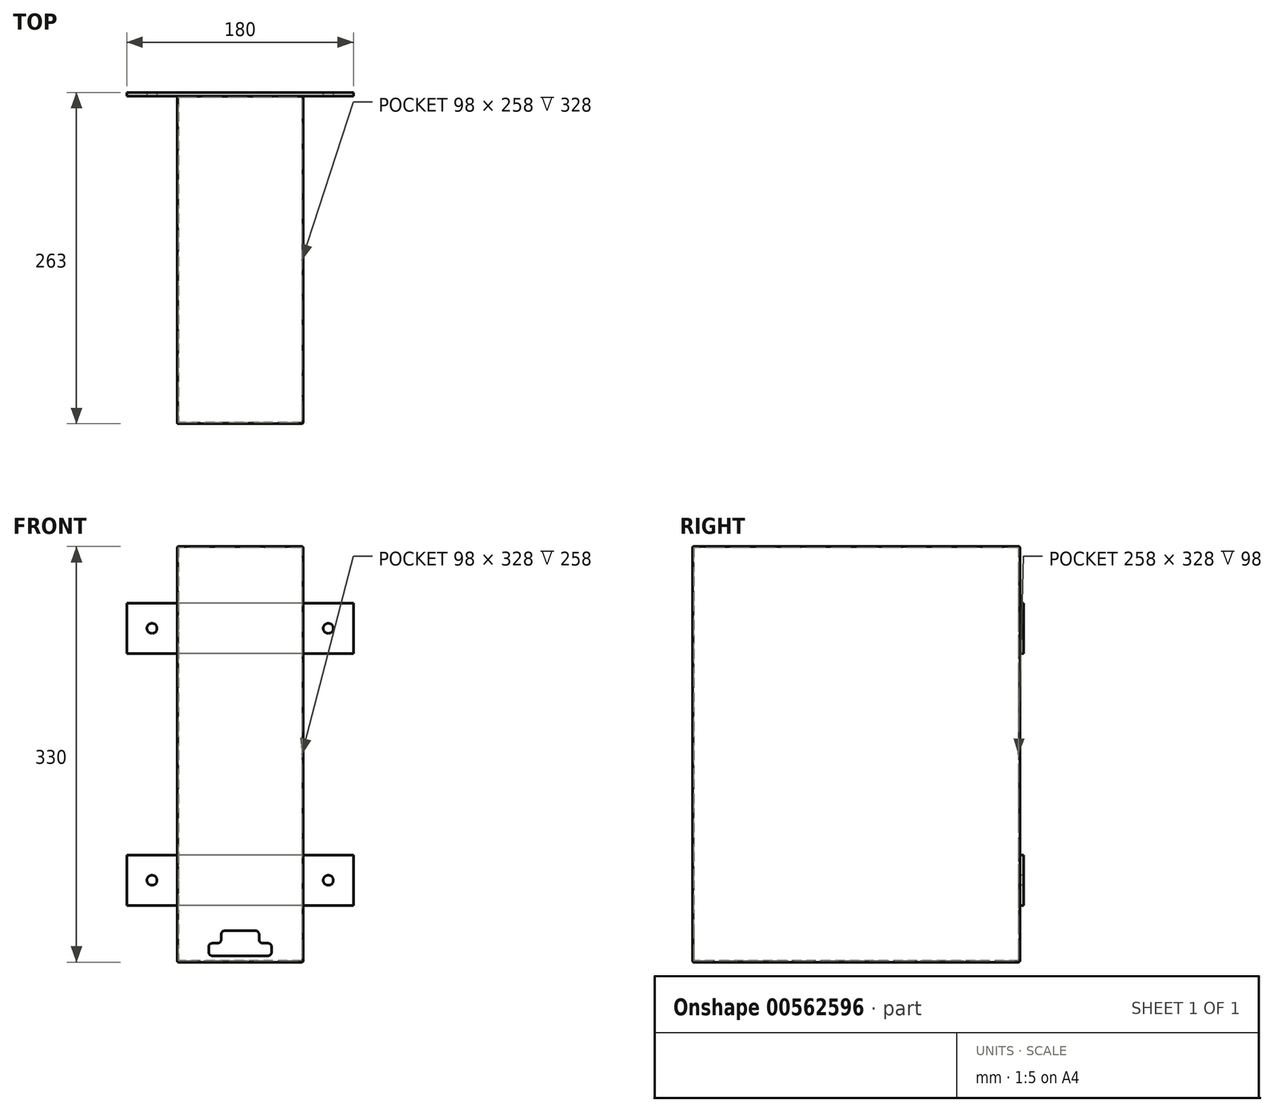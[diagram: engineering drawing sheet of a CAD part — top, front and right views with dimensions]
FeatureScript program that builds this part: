
annotation { "Feature Type Name" : "Feature", "Feature Type Description" : "" }
export const myFeature = defineFeature(function(context is Context, id is Id, definition is map)
    precondition{}
    {
        {
            var Q0;
            Q0=qCreatedBy(makeId("Top.planeOp"),FACE);
            var sketch = newSketch(context, id + "F0", { "sketchPlane" : qUnion([Q0])});
            skLineSegment(sketch, "E0.bottom", {"start": v(50, 130) * mm, "end": v(-50, 130) * mm});
            skLineSegment(sketch, "E0.top", {"start": v(50, -130) * mm, "end": v(-50, -130) * mm});
            skLineSegment(sketch, "E0.left", {"start": v(50, 130) * mm, "end": v(50, -130) * mm});
            skLineSegment(sketch, "E0.right", {"start": v(-50, 130) * mm, "end": v(-50, -130) * mm});
            skPoint(sketch, "E0.middle", {"position": v(0, 0) * mm});
            skSolve(sketch);
        }
        {
            var Q0;
            Q0=qSketchRegion(id+"F0",true);
            extrude(context, id + "F1", {"entities" : qUnion([Q0]), "endBound" : BoundingType.SYMMETRIC, "depth" : 330 * mm, "offsetDistance" : 25 * mm});
        }
        {
            var Q0;
            Q0=makeQuery(id+"F1.opExtrude","SWEPT_FACE",FACE,{"disambiguationData":[OSD([sQuery(id+"F0.wireOp",EDGE,"E0.left")])]});
            var Q1;
            Q1=makeQuery(id+"F1.opExtrude","SWEPT_FACE",FACE,{"disambiguationData":[OSD([sQuery(id+"F0.wireOp",EDGE,"E0.top")])]});
            var Q2;
            Q2=makeQuery(id+"F1.opExtrude","CAP_FACE",FACE,{"disambiguationData":[OSD([sQuery(id+"F0.wireOp",EDGE,"E0.bottom"),sQuery(id+"F0.wireOp",EDGE,"E0.top"),sQuery(id+"F0.wireOp",EDGE,"E0.left"),sQuery(id+"F0.wireOp",EDGE,"E0.right")])],"isStart":false});
            var Q3;
            Q3=makeQuery(id+"F1.opExtrude","SWEPT_FACE",FACE,{"disambiguationData":[OSD([sQuery(id+"F0.wireOp",EDGE,"E0.right")])]});
            var Q4;
            Q4=makeQuery(id+"F1.opExtrude","SWEPT_BODY",BODY,{"disambiguationData":[OSD([sQuery(id+"F0.wireOp",EDGE,"E0.bottom"),sQuery(id+"F0.wireOp",EDGE,"E0.top"),sQuery(id+"F0.wireOp",EDGE,"E0.left"),sQuery(id+"F0.wireOp",EDGE,"E0.right")])]});
            shell(context, id + "F2", {"isHollow" : true, "entities" : qUnion([Q0, Q1, Q2, Q3]), "parts" : qUnion([Q4]), "thickness" : 1 * mm});
        }
        {
            var Q0;
            Q0=makeQuery(id+"F1.opExtrude","SWEPT_FACE",FACE,{"disambiguationData":[OSD([sQuery(id+"F0.wireOp",EDGE,"E0.top")])]});
            var sketch = newSketch(context, id + "F3", { "sketchPlane" : qUnion([Q0])});
            skPoint(sketch, "E1.orphan", {"position": v(50, -165) * mm});
            skLineSegment(sketch, "E2.bottom", {"start": v(-22, -150) * mm, "end": v(-18, -150) * mm});
            skLineSegment(sketch, "E2.top", {"start": v(-22, -160) * mm, "end": v(22, -160) * mm});
            skLineSegment(sketch, "E2.left", {"start": v(-25, -153) * mm, "end": v(-25, -157) * mm});
            skLineSegment(sketch, "E2.right", {"start": v(25, -153) * mm, "end": v(25, -157) * mm});
            skLineSegment(sketch, "E3", {"start": v(-15, -147) * mm, "end": v(-15, -143) * mm});
            skLineSegment(sketch, "E4", {"start": v(-12, -140) * mm, "end": v(12, -140) * mm});
            skLineSegment(sketch, "E5", {"start": v(15, -143) * mm, "end": v(15, -147) * mm});
            skLineSegment(sketch, "E6.trimOffspring", {"start": v(18, -150) * mm, "end": v(22, -150) * mm});
            skPoint(sketch, "E7.visualSharp", {"position": v(-15, -140) * mm});
            skArc(sketch, "E7.filletArc", {"start": v(-12, -140) * mm, "mid": v(-14.12, -140.88) * mm, "end": v(-15, -143) * mm});
            skPoint(sketch, "E8.visualSharp", {"position": v(15, -140) * mm});
            skArc(sketch, "E8.filletArc", {"start": v(15, -143) * mm, "mid": v(14.12, -140.88) * mm, "end": v(12, -140) * mm});
            skPoint(sketch, "E9.visualSharp", {"position": v(15, -150) * mm});
            skArc(sketch, "E9.filletArc", {"start": v(15, -147) * mm, "mid": v(15.88, -149.12) * mm, "end": v(18, -150) * mm});
            skPoint(sketch, "E10.visualSharp", {"position": v(-15, -150) * mm});
            skArc(sketch, "E10.filletArc", {"start": v(-18, -150) * mm, "mid": v(-15.88, -149.12) * mm, "end": v(-15, -147) * mm});
            skPoint(sketch, "E11.visualSharp", {"position": v(25, -150) * mm});
            skArc(sketch, "E11.filletArc", {"start": v(25, -153) * mm, "mid": v(24.12, -150.88) * mm, "end": v(22, -150) * mm});
            skPoint(sketch, "E12.visualSharp", {"position": v(25, -160) * mm});
            skArc(sketch, "E12.filletArc", {"start": v(22, -160) * mm, "mid": v(24.12, -159.12) * mm, "end": v(25, -157) * mm});
            skPoint(sketch, "E13.visualSharp", {"position": v(-25, -160) * mm});
            skArc(sketch, "E13.filletArc", {"start": v(-25, -157) * mm, "mid": v(-24.12, -159.12) * mm, "end": v(-22, -160) * mm});
            skPoint(sketch, "E14.visualSharp", {"position": v(-25, -150) * mm});
            skArc(sketch, "E14.filletArc", {"start": v(-22, -150) * mm, "mid": v(-24.12, -150.88) * mm, "end": v(-25, -153) * mm});
            skSolve(sketch);
        }
        {
            var Q0;
            Q0=qSketchRegion(id+"F3",true);
            extrude(context, id + "F4", {"entities" : qUnion([Q0]), "operationType" : NewBodyOperationType.REMOVE, "endBound" : BoundingType.SYMMETRIC, "oppositeDirection" : true, "depth" : 440 * mm, "offsetDistance" : 25 * mm});
        }
        {
            var Q0;
            Q0=makeQuery(id+"F1.opExtrude","SWEPT_FACE",FACE,{"disambiguationData":[OSD([sQuery(id+"F0.wireOp",EDGE,"E0.left")])]});
            var Q1;
            Q1=makeQuery(id+"F1.opExtrude","CAP_FACE",FACE,{"disambiguationData":[OSD([sQuery(id+"F0.wireOp",EDGE,"E0.bottom"),sQuery(id+"F0.wireOp",EDGE,"E0.top"),sQuery(id+"F0.wireOp",EDGE,"E0.left"),sQuery(id+"F0.wireOp",EDGE,"E0.right")])],"isStart":false});
            var Q2;
            Q2=makeQuery(id+"F1.opExtrude","SWEPT_FACE",FACE,{"disambiguationData":[OSD([sQuery(id+"F0.wireOp",EDGE,"E0.right")])]});
            var Q3;
            Q3=makeQuery(id+"F1.opExtrude","CAP_FACE",FACE,{"disambiguationData":[OSD([sQuery(id+"F0.wireOp",EDGE,"E0.bottom"),sQuery(id+"F0.wireOp",EDGE,"E0.top"),sQuery(id+"F0.wireOp",EDGE,"E0.left"),sQuery(id+"F0.wireOp",EDGE,"E0.right")])],"isStart":true});
            var Q4;
            Q4=makeQuery(id+"F1.opExtrude","SWEPT_FACE",FACE,{"disambiguationData":[OSD([sQuery(id+"F0.wireOp",EDGE,"E0.bottom")])]});
            fillet(context, id + "F5", {"entities" : qUnion([Q0, Q1, Q2, Q3, Q4]), "radius" : 1 * mm, "tangentPropagation" : true, "allowEdgeOverflow" : false});
        }
        {
            var Q0;
            Q0=makeQuery(id+"F1.opExtrude","SWEPT_FACE",FACE,{"disambiguationData":[OSD([sQuery(id+"F0.wireOp",EDGE,"E0.bottom")])]});
            var sketch = newSketch(context, id + "F6", { "sketchPlane" : qUnion([Q0])});
            skLineSegment(sketch, "E15.bottom", {"start": v(-90, 120) * mm, "end": v(90, 120) * mm});
            skLineSegment(sketch, "E15.top", {"start": v(-90, 80) * mm, "end": v(90, 80) * mm});
            skLineSegment(sketch, "E15.left", {"start": v(-90, 120) * mm, "end": v(-90, 80) * mm});
            skLineSegment(sketch, "E15.right", {"start": v(90, 120) * mm, "end": v(90, 80) * mm});
            skLineSegment(sketch, "E16.bottom", {"start": v(-90, -80) * mm, "end": v(90, -80) * mm});
            skLineSegment(sketch, "E16.top", {"start": v(-90, -120) * mm, "end": v(90, -120) * mm});
            skLineSegment(sketch, "E16.left", {"start": v(-90, -80) * mm, "end": v(-90, -120) * mm});
            skLineSegment(sketch, "E16.right", {"start": v(90, -80) * mm, "end": v(90, -120) * mm});
            skCircle(sketch, "E17", {"center": v(-70, 100) * mm, "radius": 4 * mm});
            skPoint(sketch, "E17.centerSnap0", {"position": v(-90, 100) * mm});
            skCircle(sketch, "E18", {"center": v(70, 100) * mm, "radius": 4 * mm});
            skPoint(sketch, "E18.centerSnap0", {"position": v(90, 100) * mm});
            skCircle(sketch, "E19.MirrorC", {"center": v(-70, -100) * mm, "radius": 4 * mm});
            skCircle(sketch, "E20.MirrorC", {"center": v(70, -100) * mm, "radius": 4 * mm});
            skSolve(sketch);
        }
        {
            var Q0;
            Q0 = qSketchRegion(id + "F6", true);
            extrude(context, id + "F7", {"entities" : qUnion([Q0]), "operationType" : NewBodyOperationType.ADD, "depth" : 3 * mm, "offsetDistance" : 25 * mm});
        }
    });
